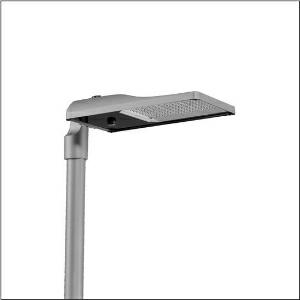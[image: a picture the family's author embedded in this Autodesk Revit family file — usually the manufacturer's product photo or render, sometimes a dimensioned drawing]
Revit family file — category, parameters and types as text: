
# Revit family: streetlight_sl_31_maxi___st0_5a_5xh8b31t08ta_8beb
name_source: partatom
category: Lighting Fixtures
units: mm (PartAtom-declared; Revit-internal decimal feet)

## family parameters
Cut with Voids When Loaded = No
Host = Face
Light Source = No
Part Type = Normal
Room Calculation Point = No
Round Connector Dimension = Use Diameter
Shared = No

## types (1)
- --- (1 x LED, 33650 lm, 228.8 W, 3000K)
    Apparent Load = 229 VA
    CIE Flux Codes = 43 76 97 100 100
    Color Rendering = 70
    Color Temperature = 3000K
    Default Elevation = 1800 mm
    Description = Streetlight SL 31 maxi D4i, Desk-Remote mast luminaire for post-top, side-entry; light control with lens of PMMA; light distribution: ST0.5a, direct asymmetric distribution, for standard-compliant lighting for roads and squares; LED: luminous flux: 33.650lm, light colour: 730, colour temperature: 3000K; luminous efficacy: 147,1lm/W; control: pre-setting: logarithmic dimming characteristic, flexible luminous flux parameterisation, time-dependent luminous flux control, constant luminous flux control, power reduction, intelligent temperature release in ECG and LED module, overheat protection; luminaire housing, of diecast aluminium, Siteco® metallic grey (DB 702S), corrosivity category C5 high according to DIN EN ISO 12944; cover of toughened safety glass, transparent, opened without tools; mast flange of diecast aluminium, Siteco® metallic grey (DB 702S), spigot size: 76/60mm, mast flange included unmounted; with cable H07RN-F 2x 1.5mm², cable length: 14,5m, connection cable pre-assembled; mains connection: 220..240V, AC, 50/60Hz; power consumption (at start of service life): 228,8W / (at end of service life): 248,7W / (with reduced operation 50%): 102,4W; protection rating (complete): IP66; insulation class (complete): insulation class II (safety insulation); impact resistance: IK09; certification: CE, ENEC, ENEC+, VDE, UKCA, ZD4i; permissible operating ambient temperature for outdoor applications: -40..+50°C; packaging unit: 1 piece

Light Distribution: ST0.5a
    Height = 79 mm
    Lamp = 1 x LED
    Lamp Light Flux = 33650 lm
    Lamp Power = 228.8 W
    Lamp count = 1
    Length = 657 mm
    Luminous efficacy = 147 lm/W
    Manufacturer = Siteco
    ModVariant = No
    Model = 5XH8B31T08TA
    Number of Poles = 1
    OnlyDefault = Yes
    Power Factor = 1
    Product Name = Streetlight SL 31 maxi | ST0.5a
    Product group = mast luminaire | pylon top
    ProductGroupID = 6100
    Protection Class = Protection class II
    Protection Degree = IP 66
    RLX_Detail_Level = 1
    RLX_Emergency_Light_Flux = 0 lm
    RLX_Emergency_Type = 0
    RLX_Emergency_Type_DB = No
    RlxData = <blob elided: 58593 chars, md5=99272a3f>
    Socket = socket
    Standby Power = 0 W
    System Light Flux = 33650 lm
    System Power = 229 W
    Type Comments = factory setting: luminous flux: 100 % | dim-lin: 254 | 802 mA
    Type Image = l_1300303.jpg
    URL = http://relux.com
    VarID = @adj_039894
    Voltage = 0 V
    Weight = 0.00 kg
    Width = 362 mm

## geometry (parser evidence)
native form markers: Blend x4, Sweep x11
no freeform markers — native parametric forms only
